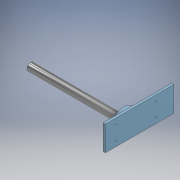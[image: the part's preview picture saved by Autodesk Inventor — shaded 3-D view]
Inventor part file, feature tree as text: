
AUTODESK INVENTOR PART (.ipt)
format: ipt  version: 2022 (Build 260153000, 153)  size: 141,312 bytes
history: native  units: mm
features: sketch x5, extrude x4, hole x1
ambient origin geometry x8: Origin, YZ Plane, XZ Plane, XY Plane, X Axis, Y Axis, Z Axis, Center Point
bodies: Solid1 (feature_tree)
feature tree (10):
  extrude  "Extrusion1"  Depth=198.0mm TaperAngle=0.0deg
  extrude  "Extrusion2"  Depth=20.0mm TaperAngle=0.0deg
  extrude  "Extrusion3"  Depth=0.75mm
  extrude  "Extrusion4"  Depth=0.0625mm
  hole  "Hole1"  [1 undecoded]
  sketch  "Sketch1"  dims[d0=600.0mm d1=0.0mm d2=198.0mm d3=0.0mm]
  sketch  "Sketch2"  dims[d4=36.0mm d5=0.0mm d6=20.0mm d7=0.0mm]
  sketch  "Sketch3"  dims[d8=6.647mm d9=18.0mm d10=4.0mm d11=2.0mm d12=90.0deg d13=8.0mm d14=20.594885mm d15=0.75mm]
  sketch  "Sketch4"  dims[d16=20.594885mm d17=0.0625mm]
  sketch  "Sketch5"  dims[d18=0.75mm d19=0.375mm]
note: 1 required parameter value undecoded (feature->parameter linkage not recoverable at this tier; creation-order binding heuristic only, values carry confidence <= 0.55)
